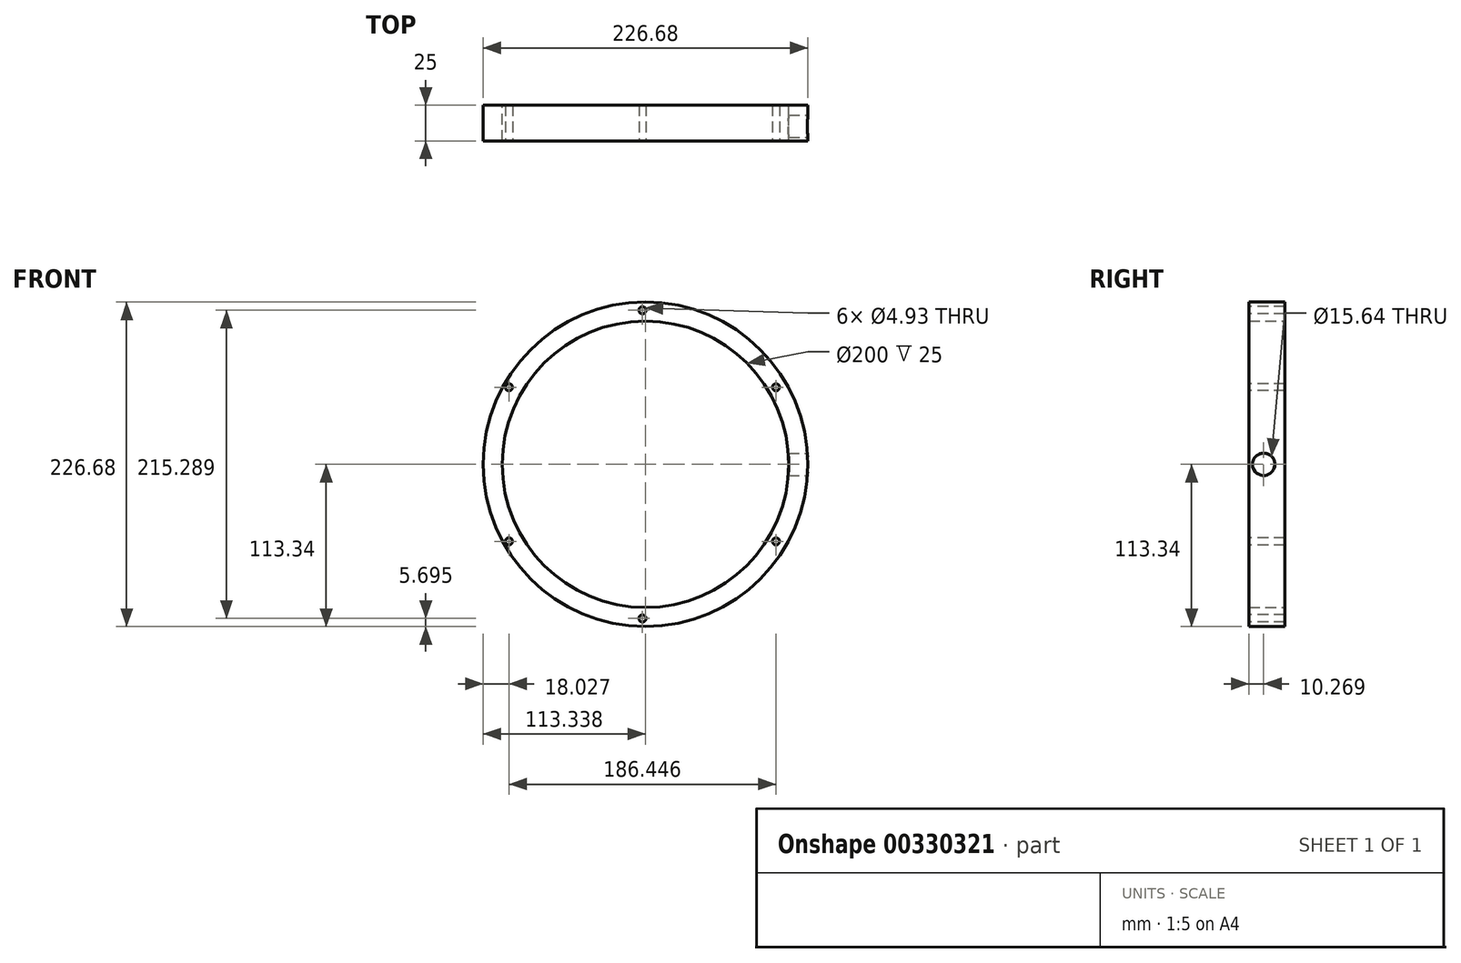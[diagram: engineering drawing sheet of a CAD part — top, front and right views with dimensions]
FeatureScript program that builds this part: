
annotation { "Feature Type Name" : "Feature", "Feature Type Description" : "" }
export const myFeature = defineFeature(function(context is Context, id is Id, definition is map)
    precondition{}
    {
        {
            var Q0;
            Q0=qCreatedBy(makeId("Front.planeOp"),FACE);
            var sketch = newSketch(context, id + "F0", { "sketchPlane" : qUnion([Q0])});
            skCircle(sketch, "E0", {"center": v(2.09, 0) * mm, "radius": 113.34 * mm});
            skCircle(sketch, "E1", {"center": v(2.09, 0) * mm, "radius": 100 * mm});
            skSolve(sketch);
        }
        {
            var Q0;
            Q0=makeQuery(id+"F0.imprint","IMPRINT",FACE,{"disambiguationData":[TD([[makeQuery(id+"F0.imprint","IMPRINT",EDGE,{"derivedFrom":sQuery(id+"F0.wireOp",EDGE,"E0")}),1.0]])]});
            extrude(context, id + "F1", {"entities" : qUnion([Q0]), "depth" : 25 * mm});
        }
        {
            var Q0;
            Q0=makeQuery(id+"F1.opExtrude","CAP_FACE",FACE,{"disambiguationData":[OSD([sQuery(id+"F0.wireOp",EDGE,"E0"),sQuery(id+"F0.wireOp",EDGE,"E1")])],"isStart":false});
            var sketch = newSketch(context, id + "F2", { "sketchPlane" : qUnion([Q0])});
            skCircle(sketch, "E2", {"center": v(0, 107.64) * mm, "radius": 2.47 * mm});
            skCircle(sketch, "E3.1.0", {"center": v(-93.22, 53.82) * mm, "radius": 2.47 * mm});
            skCircle(sketch, "E3.2.0", {"center": v(-93.22, -53.82) * mm, "radius": 2.47 * mm});
            skCircle(sketch, "E3.3.0", {"center": v(0, -107.64) * mm, "radius": 2.47 * mm});
            skCircle(sketch, "E3.4.0", {"center": v(93.22, -53.82) * mm, "radius": 2.47 * mm});
            skCircle(sketch, "E3.5.0", {"center": v(93.22, 53.82) * mm, "radius": 2.47 * mm});
            skPoint(sketch, "E3.center", {"position": v(0, 0) * mm});
            skSolve(sketch);
        }
        {
            var Q0;
            Q0 = qSketchRegion(id + "F2", true);
            extrude(context, id + "F3", {"entities" : qUnion([Q0]), "operationType" : NewBodyOperationType.REMOVE, "oppositeDirection" : true, "depth" : 25 * mm});
        }
        {
            var Q0;
            Q0=qCreatedBy(makeId("Right.planeOp"),FACE);
            cPlane(context, id + "F4", {"entities" : qUnion([Q0]), "cplaneType" : CPlaneType.OFFSET, "offset" : 121 * mm, "width" : 150 * mm, "height" : 150 * mm});
        }
        {
            var Q0;
            Q0=qCreatedBy(id+"F4.planeOp",FACE);
            var sketch = newSketch(context, id + "F5", { "sketchPlane" : qUnion([Q0])});
            skCircle(sketch, "E4", {"center": v(-14.73, 0) * mm, "radius": 7.82 * mm});
            skSolve(sketch);
        }
        {
            var Q0;
            Q0 = qSketchRegion(id + "F5", true);
            extrude(context, id + "F6", {"entities" : qUnion([Q0]), "operationType" : NewBodyOperationType.REMOVE, "oppositeDirection" : true, "depth" : 25 * mm});
        }
    });
